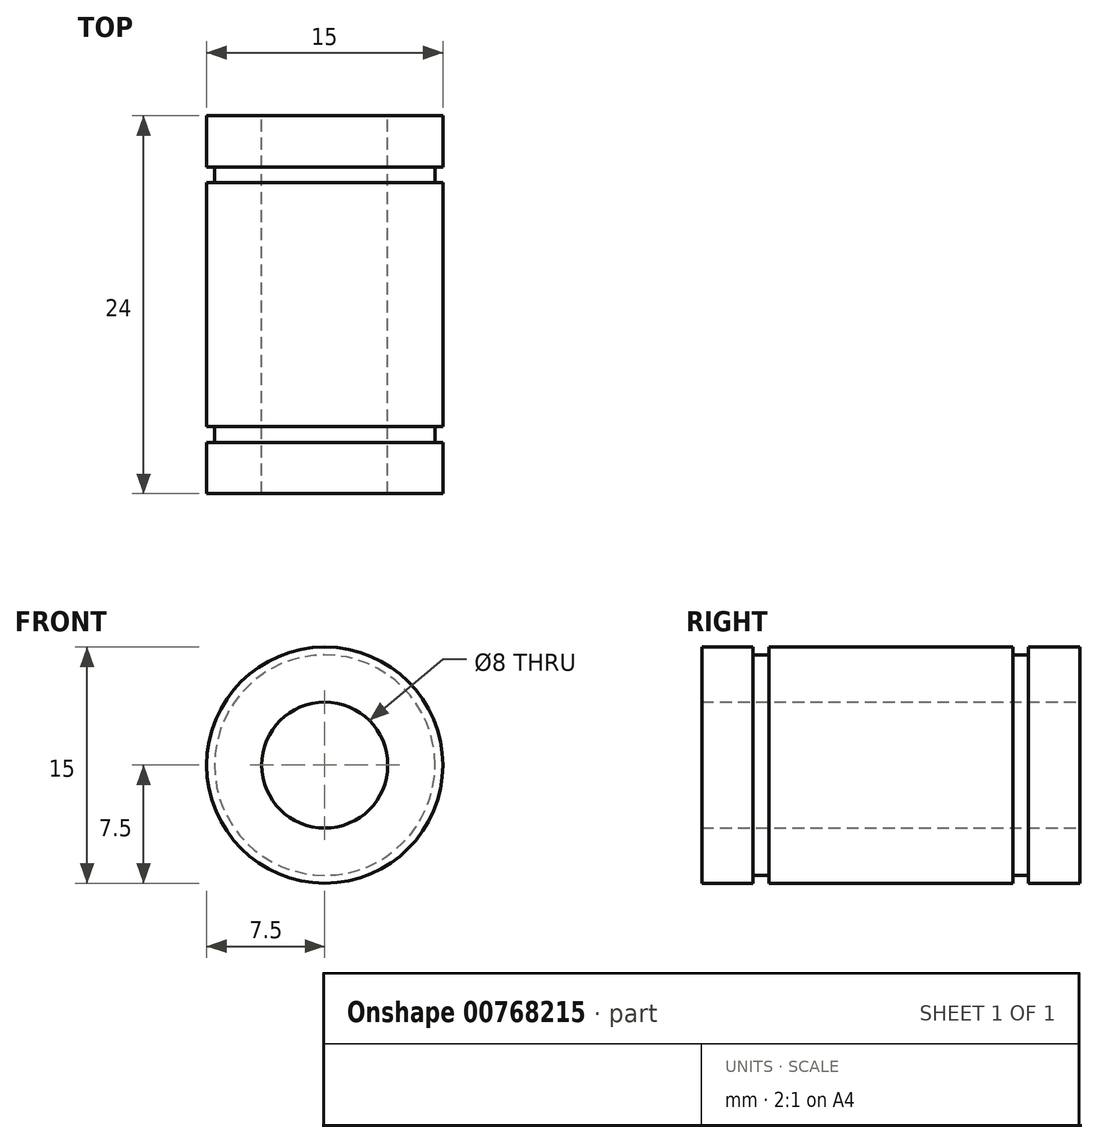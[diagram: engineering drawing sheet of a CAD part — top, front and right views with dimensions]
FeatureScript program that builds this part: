
annotation { "Feature Type Name" : "Feature", "Feature Type Description" : "" }
export const myFeature = defineFeature(function(context is Context, id is Id, definition is map)
    precondition{}
    {
        {
            var Q0;
            Q0=qCreatedBy(makeId("Front.planeOp"),FACE);
            var sketch = newSketch(context, id + "F0", { "sketchPlane" : qUnion([Q0])});
            skCircle(sketch, "E0", {"center": v(0, 0) * mm, "radius": 7.5 * mm});
            skCircle(sketch, "E1", {"center": v(0, 0) * mm, "radius": 4 * mm});
            skSolve(sketch);
        }
        {
            var Q0;
            Q0=qSketchRegion(id+"F0",true);
            extrude(context, id + "F1", {"entities" : qUnion([Q0]), "depth" : 3.25 * mm, "offsetDistance" : 25 * mm});
        }
        {
            var Q0;
            Q0=makeQuery(id+"F1.opExtrude","CAP_FACE",FACE,{"disambiguationData":[OSD([sQuery(id+"F0.wireOp",EDGE,"E0"),sQuery(id+"F0.wireOp",EDGE,"E1")])],"isStart":false});
            var sketch = newSketch(context, id + "F2", { "sketchPlane" : qUnion([Q0])});
            skCircle(sketch, "E2", {"center": v(0, 0) * mm, "radius": 7 * mm});
            skSolve(sketch);
        }
        {
            var Q0;
            Q0=makeQuery(id+"F2.imprint","IMPRINT",FACE,{"disambiguationData":[TD([[makeQuery(id+"F2.imprint","IMPRINT",EDGE,{"derivedFrom":sQuery(id+"F2.wireOp",EDGE,"E2")}),1.0]])]});
            extrude(context, id + "F3", {"entities" : qUnion([Q0]), "operationType" : NewBodyOperationType.ADD, "depth" : 1 * mm, "offsetDistance" : 25 * mm});
        }
        {
            var Q0;
            Q0=makeQuery(id+"F3.opExtrude","CAP_FACE",FACE,{"disambiguationData":[OSD([sQuery(id+"F0.wireOp",EDGE,"E1"),sQuery(id+"F2.wireOp",EDGE,"E2")])],"isStart":false});
            var sketch = newSketch(context, id + "F4", { "sketchPlane" : qUnion([Q0])});
            skCircle(sketch, "E3.0", {"center": v(0, 0) * mm, "radius": 7.5 * mm});
            skSolve(sketch);
        }
        {
            var Q0;
            Q0=makeQuery(id+"F4.imprint","IMPRINT",FACE,{"disambiguationData":[TD([[makeQuery(id+"F4.imprint","IMPRINT",EDGE,{"derivedFrom":makeQuery(id+"F3.opExtrude","CAP_EDGE",EDGE,{"disambiguationData":[OSD([sQuery(id+"F2.wireOp",EDGE,"E2")])],"isStart":false})}),1.0]])]});
            var Q1;
            Q1=makeQuery(id+"F4.imprint","IMPRINT",FACE,{"disambiguationData":[TD([[makeQuery(id+"F4.imprint","IMPRINT",EDGE,{"derivedFrom":sQuery(id+"F4.wireOp",EDGE,"E3.0")}),1.0]])]});
            extrude(context, id + "F5", {"entities" : qUnion([Q0, Q1]), "operationType" : NewBodyOperationType.ADD, "depth" : 15.5 * mm});
        }
        {
            var Q0;
            Q0=makeQuery(id+"F5.opExtrude","CAP_FACE",FACE,{"disambiguationData":[OSD([sQuery(id+"F0.wireOp",EDGE,"E1"),sQuery(id+"F4.wireOp",EDGE,"E3.0")])],"isStart":false});
            var sketch = newSketch(context, id + "F6", { "sketchPlane" : qUnion([Q0])});
            skCircle(sketch, "E4.0", {"center": v(0, 0) * mm, "radius": 7 * mm});
            skSolve(sketch);
        }
        {
            var Q0;
            Q0=makeQuery(id+"F6.imprint","IMPRINT",FACE,{"disambiguationData":[TD([[makeQuery(id+"F6.imprint","IMPRINT",EDGE,{"derivedFrom":sQuery(id+"F6.wireOp",EDGE,"E4.0")}),1.0]])]});
            extrude(context, id + "F7", {"entities" : qUnion([Q0]), "operationType" : NewBodyOperationType.ADD, "depth" : 1 * mm});
        }
        {
            var Q0;
            Q0=makeQuery(id+"F7.opExtrude","CAP_FACE",FACE,{"disambiguationData":[OSD([sQuery(id+"F0.wireOp",EDGE,"E1"),sQuery(id+"F6.wireOp",EDGE,"E4.0")])],"isStart":false});
            var sketch = newSketch(context, id + "F8", { "sketchPlane" : qUnion([Q0])});
            skCircle(sketch, "E5.0", {"center": v(0, 0) * mm, "radius": 7.5 * mm});
            skSolve(sketch);
        }
        {
            var Q0;
            Q0=makeQuery(id+"F8.imprint","IMPRINT",FACE,{"disambiguationData":[TD([[makeQuery(id+"F8.imprint","IMPRINT",EDGE,{"derivedFrom":sQuery(id+"F8.wireOp",EDGE,"E5.0")}),1.0]])]});
            var Q1;
            Q1=makeQuery(id+"F8.imprint","IMPRINT",FACE,{"disambiguationData":[TD([[makeQuery(id+"F8.imprint","IMPRINT",EDGE,{"derivedFrom":makeQuery(id+"F7.opExtrude","CAP_EDGE",EDGE,{"disambiguationData":[OSD([sQuery(id+"F6.wireOp",EDGE,"E4.0")])],"isStart":false})}),1.0]])]});
            extrude(context, id + "F9", {"entities" : qUnion([Q0, Q1]), "operationType" : NewBodyOperationType.ADD, "depth" : 3.25 * mm});
        }
    });
